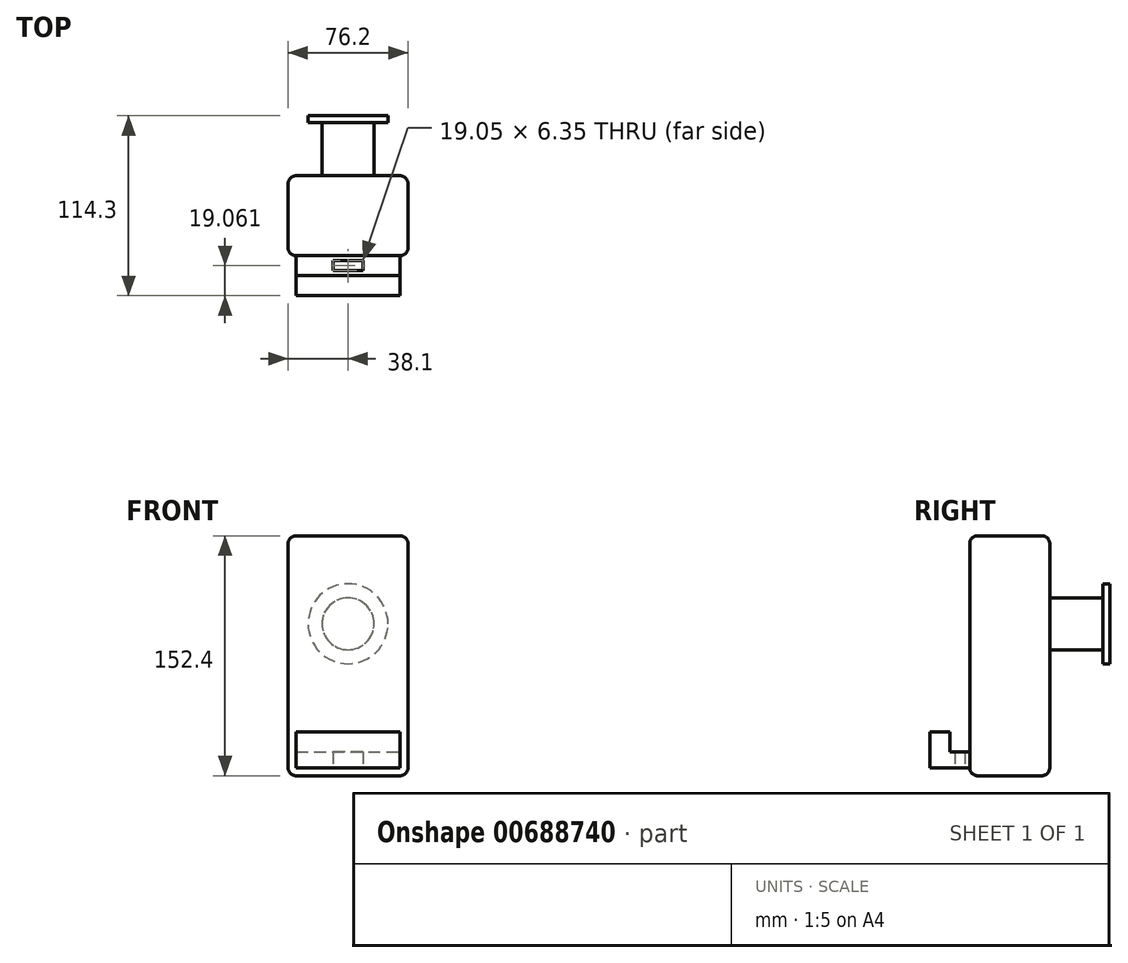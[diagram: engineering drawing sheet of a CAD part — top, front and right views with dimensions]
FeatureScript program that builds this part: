
annotation { "Feature Type Name" : "Feature", "Feature Type Description" : "" }
export const myFeature = defineFeature(function(context is Context, id is Id, definition is map)
    precondition{}
    {
        {
            var Q0;
            Q0=qCreatedBy(makeId("Front.planeOp"),FACE);
            var sketch = newSketch(context, id + "F0", { "sketchPlane" : qUnion([Q0])});
            skLineSegment(sketch, "E0", {"start": v(11.7, 134.94) * mm, "end": v(87.9, 134.94) * mm});
            skLineSegment(sketch, "E1", {"start": v(87.9, 134.94) * mm, "end": v(87.9, -17.46) * mm});
            skLineSegment(sketch, "E2", {"start": v(87.9, -17.46) * mm, "end": v(11.7, -17.46) * mm});
            skLineSegment(sketch, "E3", {"start": v(11.7, -17.46) * mm, "end": v(11.7, 134.94) * mm});
            skSolve(sketch);
        }
        {
            var Q0;
            Q0 = qSketchRegion(id + "F0", true);
            extrude(context, id + "F1", {"entities" : qUnion([Q0]), "depth" : 50.8 * mm, "offsetDistance" : 25.4 * mm});
        }
        {
            var Q0;
            Q0=makeQuery(id+"F1.opExtrude","CAP_FACE",FACE,{"disambiguationData":[OSD([sQuery(id+"F0.wireOp",EDGE,"E0"),sQuery(id+"F0.wireOp",EDGE,"E1"),sQuery(id+"F0.wireOp",EDGE,"E2"),sQuery(id+"F0.wireOp",EDGE,"E3")])],"isStart":false});
            var Q1;
            Q1=makeQuery(id+"F1.opExtrude","SWEPT_FACE",FACE,{"disambiguationData":[OSD([sQuery(id+"F0.wireOp",EDGE,"E2")])]});
            var Q2;
            Q2=makeQuery(id+"F1.opExtrude","CAP_FACE",FACE,{"disambiguationData":[OSD([sQuery(id+"F0.wireOp",EDGE,"E0"),sQuery(id+"F0.wireOp",EDGE,"E1"),sQuery(id+"F0.wireOp",EDGE,"E2"),sQuery(id+"F0.wireOp",EDGE,"E3")])],"isStart":true});
            var Q3;
            Q3=makeQuery(id+"F1.opExtrude","SWEPT_FACE",FACE,{"disambiguationData":[OSD([sQuery(id+"F0.wireOp",EDGE,"E3")])]});
            var Q4;
            Q4=makeQuery(id+"F1.opExtrude","SWEPT_FACE",FACE,{"disambiguationData":[OSD([sQuery(id+"F0.wireOp",EDGE,"E1")])]});
            fillet(context, id + "F2", {"entities" : qUnion([Q0, Q1, Q2, Q3, Q4]), "radius" : 5.08 * mm, "tangentPropagation" : true, "allowEdgeOverflow" : false});
        }
        {
            var Q0;
            Q0=makeQuery(id+"F1.opExtrude","CAP_FACE",FACE,{"disambiguationData":[OSD([sQuery(id+"F0.wireOp",EDGE,"E0"),sQuery(id+"F0.wireOp",EDGE,"E1"),sQuery(id+"F0.wireOp",EDGE,"E2"),sQuery(id+"F0.wireOp",EDGE,"E3")])],"isStart":false});
            var sketch = newSketch(context, id + "F3", { "sketchPlane" : qUnion([Q0])});
            skLineSegment(sketch, "E4", {"start": v(16.78, -2.3) * mm, "end": v(82.82, -2.3) * mm});
            skLineSegment(sketch, "E5", {"start": v(82.82, -2.3) * mm, "end": v(82.82, -12.38) * mm});
            skLineSegment(sketch, "E6", {"start": v(82.82, -12.38) * mm, "end": v(16.78, -12.38) * mm});
            skLineSegment(sketch, "E7", {"start": v(16.78, -12.38) * mm, "end": v(16.78, -2.3) * mm});
            skSolve(sketch);
        }
        {
            var Q0;
            Q0 = qSketchRegion(id + "F3", true);
            extrude(context, id + "F4", {"entities" : qUnion([Q0]), "operationType" : NewBodyOperationType.ADD, "depth" : 25.4 * mm, "offsetDistance" : 25.4 * mm});
        }
        {
            var Q0;
            Q0=makeQuery(id+"F4.opExtrude","SWEPT_FACE",FACE,{"disambiguationData":[OSD([sQuery(id+"F3.wireOp",EDGE,"E4")])]});
            var sketch = newSketch(context, id + "F5", { "sketchPlane" : qUnion([Q0])});
            skLineSegment(sketch, "E8", {"start": v(16.78, -63.5) * mm, "end": v(82.82, -63.5) * mm});
            skLineSegment(sketch, "E9", {"start": v(82.82, -63.5) * mm, "end": v(82.82, -76.2) * mm});
            skLineSegment(sketch, "E10", {"start": v(82.82, -76.2) * mm, "end": v(16.78, -76.2) * mm});
            skLineSegment(sketch, "E11", {"start": v(16.78, -76.2) * mm, "end": v(16.78, -63.5) * mm});
            skSolve(sketch);
        }
        {
            var Q0;
            Q0 = qSketchRegion(id + "F5", true);
            extrude(context, id + "F6", {"entities" : qUnion([Q0]), "operationType" : NewBodyOperationType.ADD, "depth" : 12.7 * mm, "offsetDistance" : 25.4 * mm});
        }
        {
            var Q0;
            Q0=makeQuery(id+"F4.opExtrude","SWEPT_FACE",FACE,{"disambiguationData":[OSD([sQuery(id+"F3.wireOp",EDGE,"E6")])]});
            var sketch = newSketch(context, id + "F7", { "sketchPlane" : qUnion([Q0])});
            skLineSegment(sketch, "E12.bottom", {"start": v(40.28, 53.96) * mm, "end": v(59.33, 53.96) * mm});
            skLineSegment(sketch, "E12.top", {"start": v(40.28, 60.31) * mm, "end": v(59.33, 60.31) * mm});
            skLineSegment(sketch, "E12.left", {"start": v(40.28, 53.96) * mm, "end": v(40.28, 60.31) * mm});
            skLineSegment(sketch, "E12.right", {"start": v(59.33, 53.96) * mm, "end": v(59.33, 60.31) * mm});
            skSolve(sketch);
        }
        {
            var Q0;
            Q0 = qSketchRegion(id + "F7", true);
            extrude(context, id + "F8", {"entities" : qUnion([Q0]), "operationType" : NewBodyOperationType.REMOVE, "oppositeDirection" : true, "depth" : 103.89 * mm, "offsetDistance" : 25.4 * mm});
        }
        {
            var Q0;
            Q0=makeQuery(id+"F1.opExtrude","CAP_FACE",FACE,{"disambiguationData":[OSD([sQuery(id+"F0.wireOp",EDGE,"E0"),sQuery(id+"F0.wireOp",EDGE,"E1"),sQuery(id+"F0.wireOp",EDGE,"E2"),sQuery(id+"F0.wireOp",EDGE,"E3")])],"isStart":true});
            var sketch = newSketch(context, id + "F9", { "sketchPlane" : qUnion([Q0])});
            skCircle(sketch, "E13", {"center": v(-49.8, 79.06) * mm, "radius": 16.51 * mm});
            skSolve(sketch);
        }
        {
            var Q0;
            Q0=makeQuery(id+"F9.imprint","IMPRINT",FACE,{"disambiguationData":[TD([[makeQuery(id+"F9.imprint","IMPRINT",EDGE,{"derivedFrom":sQuery(id+"F9.wireOp",EDGE,"E13")}),1.0]])]});
            extrude(context, id + "F10", {"entities" : qUnion([Q0]), "operationType" : NewBodyOperationType.ADD, "depth" : 38.1 * mm, "offsetDistance" : 25.4 * mm});
        }
        {
            var Q0;
            Q0=makeQuery(id+"F10.opExtrude","CAP_FACE",FACE,{"disambiguationData":[OSD([sQuery(id+"F9.wireOp",EDGE,"E13")])],"isStart":false});
            var sketch = newSketch(context, id + "F11", { "sketchPlane" : qUnion([Q0])});
            skCircle(sketch, "E14", {"center": v(-49.8, 79.06) * mm, "radius": 25.4 * mm});
            skSolve(sketch);
        }
        {
            var Q0;
            Q0=makeQuery(id+"F11.imprint","IMPRINT",FACE,{"disambiguationData":[TD([[makeQuery(id+"F11.imprint","IMPRINT",EDGE,{"derivedFrom":sQuery(id+"F11.wireOp",EDGE,"E14")}),1.0]])]});
            extrude(context, id + "F12", {"entities" : qUnion([Q0]), "operationType" : NewBodyOperationType.ADD, "oppositeDirection" : true, "depth" : 4.32 * mm, "offsetDistance" : 25.4 * mm});
        }
    });
